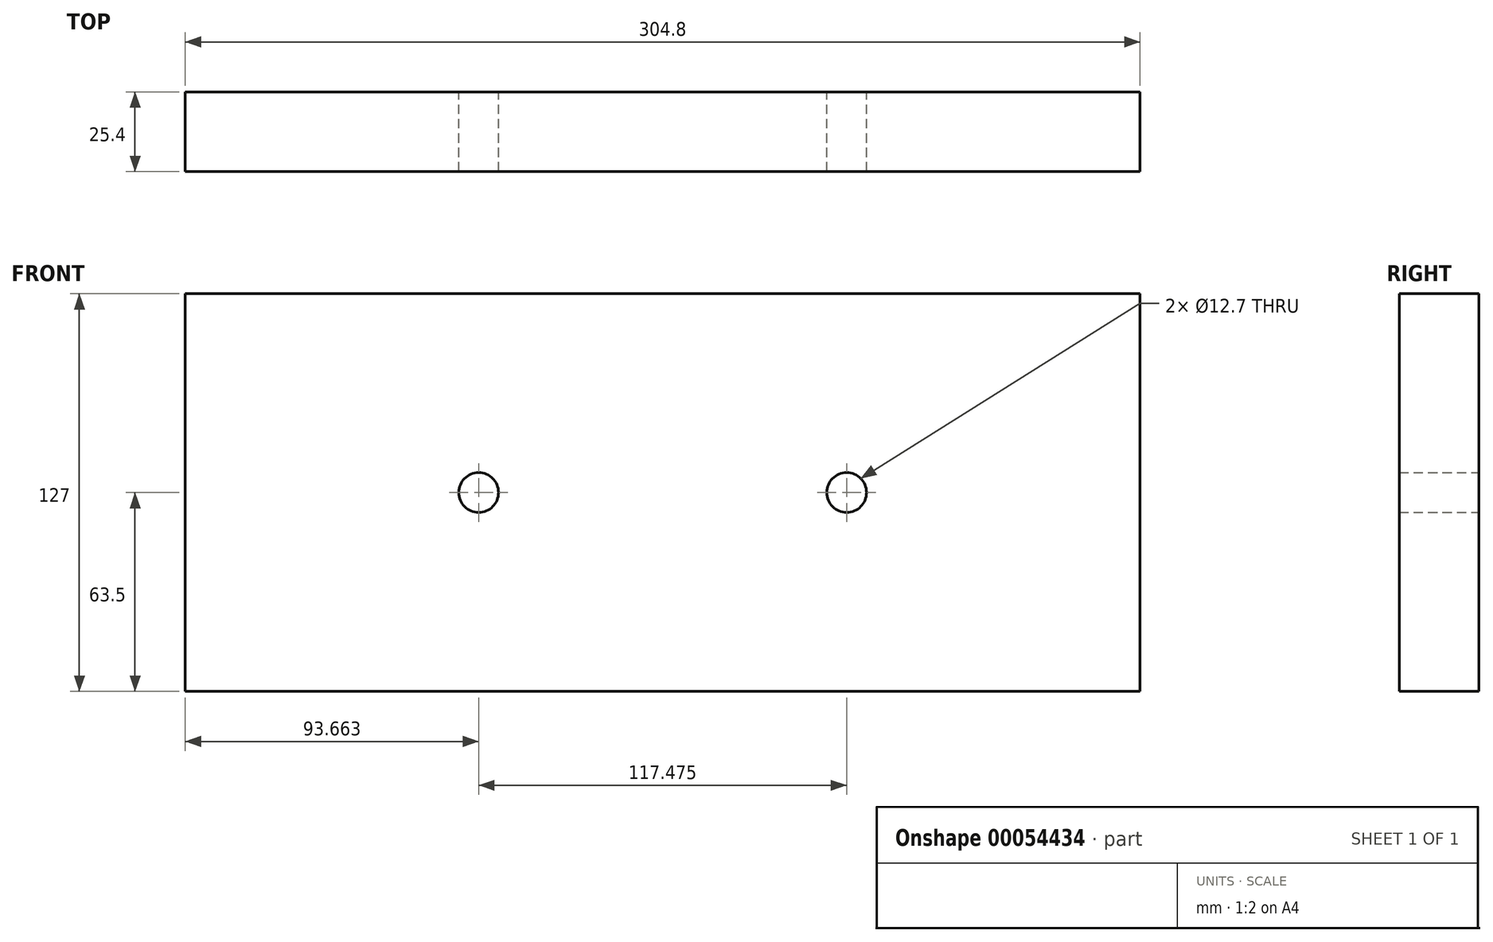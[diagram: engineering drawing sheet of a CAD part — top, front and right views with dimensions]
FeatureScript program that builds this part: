
annotation { "Feature Type Name" : "Feature", "Feature Type Description" : "" }
export const myFeature = defineFeature(function(context is Context, id is Id, definition is map)
    precondition{}
    {
        {
            var Q0;
            Q0=qCreatedBy(makeId("Front.planeOp"),FACE);
            var sketch = newSketch(context, id + "F0", { "sketchPlane" : qUnion([Q0])});
            skLineSegment(sketch, "E0.rect.bottom", {"start": v(-152.4, -63.5) * mm, "end": v(152.4, -63.5) * mm});
            skLineSegment(sketch, "E0.rect.top", {"start": v(-152.4, 63.5) * mm, "end": v(152.4, 63.5) * mm});
            skLineSegment(sketch, "E0.rect.left", {"start": v(-152.4, -63.5) * mm, "end": v(-152.4, 63.5) * mm});
            skLineSegment(sketch, "E0.rect.right", {"start": v(152.4, -63.5) * mm, "end": v(152.4, 63.5) * mm});
            skPoint(sketch, "E0.rect.middle", {"position": v(0, 0) * mm});
            skCircle(sketch, "E1", {"center": v(-58.74, 0) * mm, "radius": 6.35 * mm});
            skLineSegment(sketch, "E2", {"start": v(0, 63.5) * mm, "end": v(0, -63.5) * mm, "construction": true});
            skCircle(sketch, "E3.MirrorC", {"center": v(58.74, 0) * mm, "radius": 6.35 * mm});
            skSolve(sketch);
        }
        {
            var Q0;
            Q0=makeQuery(id+"F0.imprint","IMPRINT",FACE,{"disambiguationData":[TD([[makeQuery(id+"F0.imprint","IMPRINT",EDGE,{"derivedFrom":sQuery(id+"F0.wireOp",EDGE,"E0.rect.bottom")}),1.0]])]});
            extrude(context, id + "F1", {"entities" : qUnion([Q0]), "depth" : 25.4 * mm});
        }
    });
